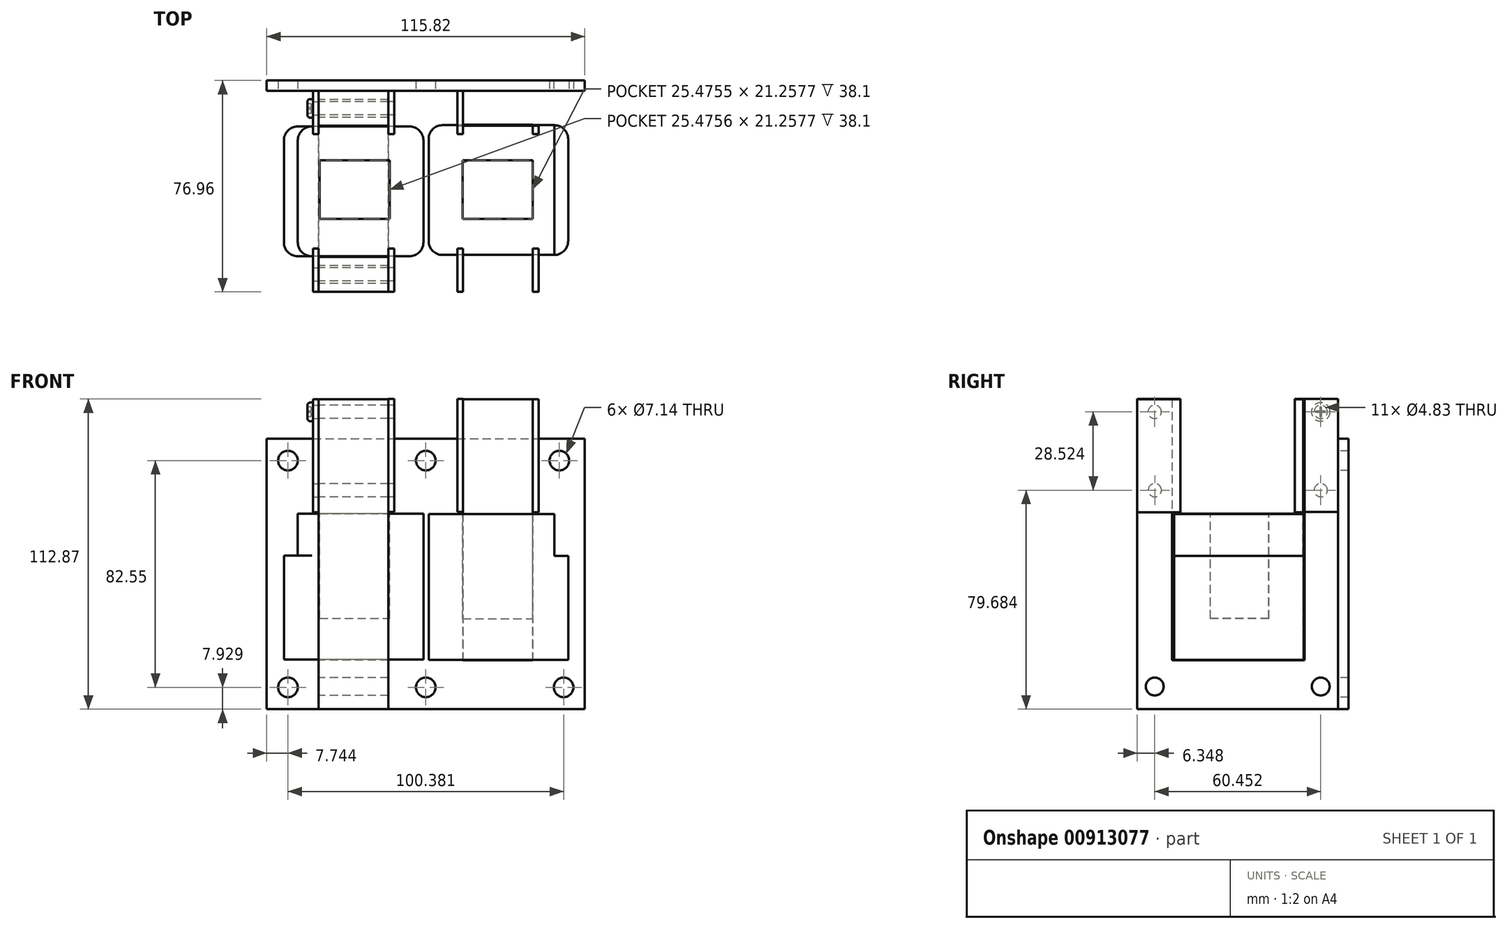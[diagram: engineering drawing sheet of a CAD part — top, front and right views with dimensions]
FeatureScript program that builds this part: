
annotation { "Feature Type Name" : "Feature", "Feature Type Description" : "" }
export const myFeature = defineFeature(function(context is Context, id is Id, definition is map)
    precondition{}
    {
        {
            var Q0;
            Q0=qCreatedBy(makeId("Front.planeOp"),FACE);
            var sketch = newSketch(context, id + "F0", { "sketchPlane" : qUnion([Q0])});
            skLineSegment(sketch, "E0", {"start": v(-55.41, 38.66) * mm, "end": v(60.41, 38.66) * mm});
            skLineSegment(sketch, "E1", {"start": v(60.41, 38.66) * mm, "end": v(60.41, -59.74) * mm});
            skLineSegment(sketch, "E2", {"start": v(60.41, -59.74) * mm, "end": v(-55.41, -59.74) * mm});
            skLineSegment(sketch, "E3", {"start": v(-55.41, 38.66) * mm, "end": v(-55.41, -59.74) * mm});
            skCircle(sketch, "E4", {"center": v(-47.67, -51.81) * mm, "radius": 3.57 * mm});
            skCircle(sketch, "E5", {"center": v(2.52, -51.81) * mm, "radius": 3.57 * mm});
            skCircle(sketch, "E6", {"center": v(52.71, -51.81) * mm, "radius": 3.57 * mm});
            skCircle(sketch, "E7", {"center": v(-47.67, 30.74) * mm, "radius": 3.57 * mm});
            skCircle(sketch, "E8", {"center": v(2.52, 30.74) * mm, "radius": 3.57 * mm});
            skCircle(sketch, "E9", {"center": v(51.17, 30.74) * mm, "radius": 3.57 * mm});
            skLineSegment(sketch, "E10.bottom", {"start": v(-36.46, -59.74) * mm, "end": v(-11.06, -59.74) * mm});
            skLineSegment(sketch, "E10.top", {"start": v(-36.46, 53.04) * mm, "end": v(-11.06, 53.04) * mm});
            skLineSegment(sketch, "E10.left", {"start": v(-36.46, -59.74) * mm, "end": v(-36.46, 53.04) * mm});
            skLineSegment(sketch, "E10.right", {"start": v(-11.06, -59.74) * mm, "end": v(-11.06, 53.04) * mm});
            skLineSegment(sketch, "E11.bottom", {"start": v(16.11, -59.74) * mm, "end": v(41.51, -59.74) * mm});
            skLineSegment(sketch, "E11.top", {"start": v(16.11, 53.04) * mm, "end": v(41.51, 53.04) * mm});
            skLineSegment(sketch, "E11.left", {"start": v(16.11, -59.74) * mm, "end": v(16.11, 53.04) * mm});
            skLineSegment(sketch, "E11.right", {"start": v(41.51, -59.74) * mm, "end": v(41.51, 53.04) * mm});
            skSolve(sketch);
        }
        {
            var Q0;
            {var subQ5=sQuery(id+"F0.wireOp",EDGE,"E10.top");Q0=makeQuery(id+"F0.imprint","IMPRINT",FACE,{"disambiguationData":[TD([[makeQuery(id+"F0.imprint","IMPRINT",EDGE,{"derivedFrom":subQ5}),-1.0]])]});}
            var Q1;
            {var subQ0=sQuery(id+"F0.wireOp",EDGE,"E10.right");var subQ1=sQuery(id+"F0.wireOp",EDGE,"E0");var subQ2=makeQuery(id+"F0.imprint","INTERSECT",VERTEX,{"derivedFrom":[subQ1,subQ0]});Q1=makeQuery(id+"F0.imprint","IMPRINT",FACE,{"disambiguationData":[TD([[makeQuery(id+"F0.imprint","IMPRINT",EDGE,{"disambiguationData":[TD([[subQ2,1.0]])],"derivedFrom":subQ1}),-1.0]])]});}
            var Q2;
            {var subQ0=sQuery(id+"F0.wireOp",EDGE,"E11.left");var subQ1=sQuery(id+"F0.wireOp",EDGE,"E0");var subQ2=makeQuery(id+"F0.imprint","INTERSECT",VERTEX,{"derivedFrom":[subQ1,subQ0]});Q2=makeQuery(id+"F0.imprint","IMPRINT",FACE,{"disambiguationData":[TD([[makeQuery(id+"F0.imprint","IMPRINT",EDGE,{"disambiguationData":[TD([[subQ2,-1.0]])],"derivedFrom":subQ1}),-1.0]])]});}
            var Q3;
            {var subQ5=sQuery(id+"F0.wireOp",EDGE,"E11.top");Q3=makeQuery(id+"F0.imprint","IMPRINT",FACE,{"disambiguationData":[TD([[makeQuery(id+"F0.imprint","IMPRINT",EDGE,{"derivedFrom":subQ5}),-1.0]])]});}
            extrude(context, id + "F1", {"entities" : qUnion([Q0, Q1, Q2, Q3]), "depth" : 73.15 * mm, "offsetDistance" : 25.4 * mm});
        }
        {
            var Q0;
            Q0=makeQuery(id+"F0.imprint","IMPRINT",FACE,{"disambiguationData":[TD([[makeQuery(id+"F0.imprint","IMPRINT",EDGE,{"derivedFrom":sQuery(id+"F0.wireOp",EDGE,"E5")}),-1.0]])]});
            var Q1;
            {var subQ1=sQuery(id+"F0.wireOp",EDGE,"E1");Q1=makeQuery(id+"F0.imprint","IMPRINT",FACE,{"disambiguationData":[TD([[makeQuery(id+"F0.imprint","IMPRINT",EDGE,{"derivedFrom":subQ1}),-1.0]])]});}
            var Q2;
            {var subQ0=sQuery(id+"F0.wireOp",EDGE,"E11.left");var subQ1=sQuery(id+"F0.wireOp",EDGE,"E0");var subQ2=makeQuery(id+"F0.imprint","INTERSECT",VERTEX,{"derivedFrom":[subQ1,subQ0]});Q2=makeQuery(id+"F0.imprint","IMPRINT",FACE,{"disambiguationData":[TD([[makeQuery(id+"F0.imprint","IMPRINT",EDGE,{"disambiguationData":[TD([[subQ2,-1.0]])],"derivedFrom":subQ1}),-1.0]])]});}
            var Q3;
            {var subQ0=sQuery(id+"F0.wireOp",EDGE,"E10.right");var subQ1=sQuery(id+"F0.wireOp",EDGE,"E0");var subQ2=makeQuery(id+"F0.imprint","INTERSECT",VERTEX,{"derivedFrom":[subQ1,subQ0]});Q3=makeQuery(id+"F0.imprint","IMPRINT",FACE,{"disambiguationData":[TD([[makeQuery(id+"F0.imprint","IMPRINT",EDGE,{"disambiguationData":[TD([[subQ2,1.0]])],"derivedFrom":subQ1}),-1.0]])]});}
            var Q4;
            {var subQ0=sQuery(id+"F0.wireOp",EDGE,"E3");Q4=makeQuery(id+"F0.imprint","IMPRINT",FACE,{"disambiguationData":[TD([[makeQuery(id+"F0.imprint","IMPRINT",EDGE,{"derivedFrom":subQ0}),1.0]])]});}
            extrude(context, id + "F2", {"entities" : qUnion([Q0, Q1, Q2, Q3, Q4]), "oppositeDirection" : true, "depth" : 3.8 * mm, "offsetDistance" : 25.4 * mm});
        }
        {
            var Q0;
            Q0=makeQuery(id+"F1.opExtrude","SWEPT_FACE",FACE,{"disambiguationData":[OSD([sQuery(id+"F0.wireOp",EDGE,"E10.left")])]});
            var sketch = newSketch(context, id + "F3", { "sketchPlane" : qUnion([Q0])});
            skLineSegment(sketch, "E12", {"start": v(12.7, 53.04) * mm, "end": v(12.7, -41.96) * mm});
            skLineSegment(sketch, "E13", {"start": v(12.7, -41.96) * mm, "end": v(60.45, -41.96) * mm});
            skLineSegment(sketch, "E14", {"start": v(60.45, 53.04) * mm, "end": v(60.45, -41.96) * mm});
            skLineSegment(sketch, "E15", {"start": v(60.45, 53.04) * mm, "end": v(12.7, 53.04) * mm});
            skLineSegment(sketch, "E16", {"start": v(12.7, 53.04) * mm, "end": v(60.45, 53.04) * mm});
            skCircle(sketch, "E17", {"center": v(6.35, 48.47) * mm, "radius": 2.41 * mm});
            skCircle(sketch, "E18", {"center": v(66.8, 48.47) * mm, "radius": 2.41 * mm});
            skCircle(sketch, "E19", {"center": v(6.35, 19.94) * mm, "radius": 2.41 * mm});
            skCircle(sketch, "E20", {"center": v(66.75, 19.94) * mm, "radius": 2.41 * mm});
            skCircle(sketch, "E21", {"center": v(6.35, -51.5) * mm, "radius": 3.25 * mm});
            skCircle(sketch, "E22", {"center": v(66.8, -51.5) * mm, "radius": 3.25 * mm});
            skSolve(sketch);
        }
        {
            var Q0;
            Q0=makeQuery(id+"F3.imprint","IMPRINT",FACE,{"disambiguationData":[TD([[makeQuery(id+"F3.imprint","IMPRINT",EDGE,{"derivedFrom":sQuery(id+"F3.wireOp",EDGE,"E12")}),1.0]])]});
            var Q1;
            Q1=makeQuery(id+"F3.imprint","IMPRINT",FACE,{"disambiguationData":[TD([[makeQuery(id+"F3.imprint","IMPRINT",EDGE,{"derivedFrom":sQuery(id+"F3.wireOp",EDGE,"E19")}),1.0]])]});
            var Q2;
            Q2=makeQuery(id+"F3.imprint","IMPRINT",FACE,{"disambiguationData":[TD([[makeQuery(id+"F3.imprint","IMPRINT",EDGE,{"derivedFrom":sQuery(id+"F3.wireOp",EDGE,"E20")}),1.0]])]});
            var Q3;
            Q3=makeQuery(id+"F3.imprint","IMPRINT",FACE,{"disambiguationData":[TD([[makeQuery(id+"F3.imprint","IMPRINT",EDGE,{"derivedFrom":sQuery(id+"F3.wireOp",EDGE,"E18")}),1.0]])]});
            var Q4;
            Q4=makeQuery(id+"F3.imprint","IMPRINT",FACE,{"disambiguationData":[TD([[makeQuery(id+"F3.imprint","IMPRINT",EDGE,{"derivedFrom":sQuery(id+"F3.wireOp",EDGE,"E17")}),1.0]])]});
            var Q5;
            Q5=makeQuery(id+"F3.imprint","IMPRINT",FACE,{"disambiguationData":[TD([[makeQuery(id+"F3.imprint","IMPRINT",EDGE,{"derivedFrom":sQuery(id+"F3.wireOp",EDGE,"E21")}),1.0]])]});
            var Q6;
            Q6=makeQuery(id+"F3.imprint","IMPRINT",FACE,{"disambiguationData":[TD([[makeQuery(id+"F3.imprint","IMPRINT",EDGE,{"derivedFrom":sQuery(id+"F3.wireOp",EDGE,"E22")}),1.0]])]});
            extrude(context, id + "F4", {"entities" : qUnion([Q0, Q1, Q2, Q3, Q4, Q5, Q6]), "operationType" : NewBodyOperationType.REMOVE, "endBound" : BoundingType.THROUGH_ALL, "oppositeDirection" : true, "depth" : 50.8 * mm, "offsetDistance" : 25.4 * mm});
        }
        {
            var Q0;
            Q0=makeQuery(id+"F1.opExtrude","SWEPT_FACE",FACE,{"disambiguationData":[OSD([sQuery(id+"F0.wireOp",EDGE,"E11.right")])]});
            var sketch = newSketch(context, id + "F5", { "sketchPlane" : qUnion([Q0])});
            skLineSegment(sketch, "E23", {"start": v(-60, 53.04) * mm, "end": v(-60, -41.96) * mm});
            skLineSegment(sketch, "E24", {"start": v(-60, -41.96) * mm, "end": v(-12.26, -41.96) * mm});
            skLineSegment(sketch, "E25", {"start": v(-12.26, -41.96) * mm, "end": v(-12.26, 53.04) * mm});
            skLineSegment(sketch, "E26", {"start": v(-12.26, 53.04) * mm, "end": v(-60, 53.04) * mm});
            skCircle(sketch, "E27", {"center": v(-66.8, 48.47) * mm, "radius": 2.41 * mm});
            skCircle(sketch, "E28", {"center": v(-6.35, 48.47) * mm, "radius": 2.41 * mm});
            skCircle(sketch, "E29", {"center": v(-66.8, 19.94) * mm, "radius": 2.41 * mm});
            skCircle(sketch, "E30", {"center": v(-6.35, 19.94) * mm, "radius": 2.41 * mm});
            skCircle(sketch, "E31", {"center": v(-66.8, -51.5) * mm, "radius": 3.25 * mm});
            skCircle(sketch, "E32", {"center": v(-6.35, -51.5) * mm, "radius": 3.25 * mm});
            skSolve(sketch);
        }
        {
            var Q0;
            Q0=makeQuery(id+"F5.imprint","IMPRINT",FACE,{"disambiguationData":[TD([[makeQuery(id+"F5.imprint","IMPRINT",EDGE,{"derivedFrom":sQuery(id+"F5.wireOp",EDGE,"E27")}),1.0]])]});
            var Q1;
            Q1=makeQuery(id+"F5.imprint","IMPRINT",FACE,{"disambiguationData":[TD([[makeQuery(id+"F5.imprint","IMPRINT",EDGE,{"derivedFrom":sQuery(id+"F5.wireOp",EDGE,"E29")}),1.0]])]});
            var Q2;
            Q2=makeQuery(id+"F5.imprint","IMPRINT",FACE,{"disambiguationData":[TD([[makeQuery(id+"F5.imprint","IMPRINT",EDGE,{"derivedFrom":sQuery(id+"F5.wireOp",EDGE,"E31")}),1.0]])]});
            var Q3;
            Q3=makeQuery(id+"F5.imprint","IMPRINT",FACE,{"disambiguationData":[TD([[makeQuery(id+"F5.imprint","IMPRINT",EDGE,{"derivedFrom":sQuery(id+"F5.wireOp",EDGE,"E32")}),1.0]])]});
            var Q4;
            Q4=makeQuery(id+"F5.imprint","IMPRINT",FACE,{"disambiguationData":[TD([[makeQuery(id+"F5.imprint","IMPRINT",EDGE,{"derivedFrom":sQuery(id+"F5.wireOp",EDGE,"E30")}),1.0]])]});
            var Q5;
            Q5=makeQuery(id+"F5.imprint","IMPRINT",FACE,{"disambiguationData":[TD([[makeQuery(id+"F5.imprint","IMPRINT",EDGE,{"derivedFrom":sQuery(id+"F5.wireOp",EDGE,"E28")}),1.0]])]});
            var Q6;
            Q6=makeQuery(id+"F5.imprint","IMPRINT",FACE,{"disambiguationData":[TD([[makeQuery(id+"F5.imprint","IMPRINT",EDGE,{"derivedFrom":sQuery(id+"F5.wireOp",EDGE,"E23")}),1.0]])]});
            extrude(context, id + "F6", {"entities" : qUnion([Q0, Q1, Q2, Q3, Q4, Q5, Q6]), "operationType" : NewBodyOperationType.REMOVE, "oppositeDirection" : true, "depth" : 25.4 * mm, "offsetDistance" : 25.4 * mm});
        }
        {
            var Q0;
            Q0=qCreatedBy(makeId("Right.planeOp"),FACE);
            cPlane(context, id + "F7", {"entities" : qUnion([Q0]), "cplaneType" : CPlaneType.OFFSET, "offset" : 23.75 * mm, "oppositeDirection" : true, "width" : 152.4 * mm, "height" : 152.4 * mm});
        }
        {
            var Q0;
            Q0=qCreatedBy(id+"F7.planeOp",FACE);
            var sketch = newSketch(context, id + "F8", { "sketchPlane" : qUnion([Q0])});
            skLineSegment(sketch, "E33.bottom", {"start": v(-12.93, 11.43) * mm, "end": v(-60.18, 11.43) * mm});
            skLineSegment(sketch, "E33.top", {"start": v(-12.93, -41.66) * mm, "end": v(-60.18, -41.66) * mm});
            skLineSegment(sketch, "E33.left", {"start": v(-12.93, 11.43) * mm, "end": v(-12.93, -41.66) * mm});
            skLineSegment(sketch, "E33.right", {"start": v(-60.18, 11.43) * mm, "end": v(-60.18, -41.66) * mm});
            skSolve(sketch);
        }
        {
            var Q0;
            Q0=makeQuery(id+"F8.imprint","IMPRINT",FACE,{"disambiguationData":[TD([[makeQuery(id+"F8.imprint","IMPRINT",EDGE,{"derivedFrom":sQuery(id+"F8.wireOp",EDGE,"E33.bottom")}),1.0]])]});
            extrude(context, id + "F9", {"entities" : qUnion([Q0]), "endBound" : BoundingType.SYMMETRIC, "depth" : 50.8 * mm, "offsetDistance" : 25.4 * mm});
        }
        {
            var Q0;
            Q0=makeQuery(id+"F9.opExtrude","CAP_FACE",FACE,{"disambiguationData":[OSD([sQuery(id+"F8.wireOp",EDGE,"E33.bottom"),sQuery(id+"F8.wireOp",EDGE,"E33.top"),sQuery(id+"F8.wireOp",EDGE,"E33.left"),sQuery(id+"F8.wireOp",EDGE,"E33.right")])],"isStart":true});
            var sketch = newSketch(context, id + "F10", { "sketchPlane" : qUnion([Q0])});
            skLineSegment(sketch, "E34.bottom", {"start": v(12.92, 11.43) * mm, "end": v(60.23, 11.43) * mm});
            skLineSegment(sketch, "E34.top", {"start": v(12.92, -3.8) * mm, "end": v(60.23, -3.8) * mm});
            skLineSegment(sketch, "E34.left", {"start": v(12.92, 11.43) * mm, "end": v(12.92, -3.8) * mm});
            skLineSegment(sketch, "E34.right", {"start": v(60.23, 11.43) * mm, "end": v(60.23, -3.8) * mm});
            skSolve(sketch);
        }
        {
            var Q0;
            Q0=makeQuery(id+"F10.imprint","IMPRINT",FACE,{"disambiguationData":[TD([[makeQuery(id+"F10.imprint","IMPRINT",EDGE,{"derivedFrom":sQuery(id+"F10.wireOp",EDGE,"E34.bottom")}),-1.0]])]});
            extrude(context, id + "F11", {"entities" : qUnion([Q0]), "operationType" : NewBodyOperationType.REMOVE, "oppositeDirection" : true, "depth" : 5.08 * mm, "offsetDistance" : 25.4 * mm});
        }
        {
            var Q0;
            Q0=makeQuery(id+"F9.opExtrude","CAP_EDGE",EDGE,{"disambiguationData":[OSD([sQuery(id+"F8.wireOp",EDGE,"E33.left")])],"isStart":true});
            var Q1;
            Q1=makeQuery(id+"F9.opExtrude","CAP_EDGE",EDGE,{"disambiguationData":[OSD([sQuery(id+"F8.wireOp",EDGE,"E33.right")])],"isStart":true});
            var Q2;
            Q2=makeQuery(id+"F9.opExtrude","CAP_EDGE",EDGE,{"disambiguationData":[OSD([sQuery(id+"F8.wireOp",EDGE,"E33.right")])],"isStart":false});
            var Q3;
            Q3=makeQuery(id+"F9.opExtrude","CAP_EDGE",EDGE,{"disambiguationData":[OSD([sQuery(id+"F8.wireOp",EDGE,"E33.left")])],"isStart":false});
            var Q4;
            Q4=makeQuery(id+"F11.boolean.opBoolean","INTERSECT",EDGE,{"derivedFrom":[makeQuery(id+"F9.opExtrude","SWEPT_FACE",FACE,{"disambiguationData":[OSD([sQuery(id+"F8.wireOp",EDGE,"E33.left")])]}),makeQuery(id+"F11.opExtrude","CAP_FACE",FACE,{"disambiguationData":[OSD([sQuery(id+"F10.wireOp",EDGE,"E34.bottom"),sQuery(id+"F10.wireOp",EDGE,"E34.top"),sQuery(id+"F10.wireOp",EDGE,"E34.left"),sQuery(id+"F10.wireOp",EDGE,"E34.right")])],"isStart":false})]});
            var Q5;
            Q5=makeQuery(id+"F11.boolean.opBoolean","INTERSECT",EDGE,{"derivedFrom":[makeQuery(id+"F9.opExtrude","SWEPT_FACE",FACE,{"disambiguationData":[OSD([sQuery(id+"F8.wireOp",EDGE,"E33.right")])]}),makeQuery(id+"F11.opExtrude","CAP_FACE",FACE,{"disambiguationData":[OSD([sQuery(id+"F10.wireOp",EDGE,"E34.bottom"),sQuery(id+"F10.wireOp",EDGE,"E34.top"),sQuery(id+"F10.wireOp",EDGE,"E34.left"),sQuery(id+"F10.wireOp",EDGE,"E34.right")])],"isStart":false})]});
            fillet(context, id + "F12", {"entities" : qUnion([Q0, Q1, Q2, Q3, Q4, Q5]), "radius" : 5.08 * mm, "tangentPropagation" : true, "allowEdgeOverflow" : false});
        }
        {
            var Q0;
            Q0=makeQuery(id+"F9.opExtrude","SWEPT_FACE",FACE,{"disambiguationData":[OSD([sQuery(id+"F8.wireOp",EDGE,"E33.bottom")])]});
            var sketch = newSketch(context, id + "F13", { "sketchPlane" : qUnion([Q0])});
            skLineSegment(sketch, "E35.bottom", {"start": v(-36.13, -25.29) * mm, "end": v(-10.65, -25.29) * mm});
            skLineSegment(sketch, "E35.top", {"start": v(-36.13, -46.55) * mm, "end": v(-10.65, -46.55) * mm});
            skLineSegment(sketch, "E35.left", {"start": v(-36.13, -25.29) * mm, "end": v(-36.13, -46.55) * mm});
            skLineSegment(sketch, "E35.right", {"start": v(-10.65, -25.29) * mm, "end": v(-10.65, -46.55) * mm});
            skSolve(sketch);
        }
        {
            var Q0;
            Q0=makeQuery(id+"F13.imprint","IMPRINT",FACE,{"disambiguationData":[TD([[makeQuery(id+"F13.imprint","IMPRINT",EDGE,{"derivedFrom":sQuery(id+"F13.wireOp",EDGE,"E35.bottom")}),-1.0]])]});
            extrude(context, id + "F14", {"entities" : qUnion([Q0]), "operationType" : NewBodyOperationType.REMOVE, "oppositeDirection" : true, "depth" : 38.1 * mm, "offsetDistance" : 25.4 * mm});
        }
        {
            var Q0;
            Q0=qCreatedBy(makeId("Right.planeOp"),FACE);
            cPlane(context, id + "F15", {"entities" : qUnion([Q0]), "cplaneType" : CPlaneType.OFFSET, "offset" : 28.96 * mm, "width" : 152.4 * mm, "height" : 152.4 * mm});
        }
        {
            var Q0;
            Q0=qCreatedBy(id+"F15.planeOp",FACE);
            var sketch = newSketch(context, id + "F16", { "sketchPlane" : qUnion([Q0])});
            skLineSegment(sketch, "E36.bottom", {"start": v(-12.45, 11.3) * mm, "end": v(-59.7, 11.3) * mm});
            skLineSegment(sketch, "E36.top", {"start": v(-12.45, -41.78) * mm, "end": v(-59.7, -41.78) * mm});
            skLineSegment(sketch, "E36.left", {"start": v(-12.45, 11.3) * mm, "end": v(-12.45, -41.78) * mm});
            skLineSegment(sketch, "E36.right", {"start": v(-59.7, 11.3) * mm, "end": v(-59.7, -41.78) * mm});
            skSolve(sketch);
        }
        {
            var Q0;
            Q0=makeQuery(id+"F16.imprint","IMPRINT",FACE,{"disambiguationData":[TD([[makeQuery(id+"F16.imprint","IMPRINT",EDGE,{"derivedFrom":sQuery(id+"F16.wireOp",EDGE,"E36.bottom")}),1.0]])]});
            extrude(context, id + "F17", {"entities" : qUnion([Q0]), "endBound" : BoundingType.SYMMETRIC, "depth" : 50.8 * mm, "offsetDistance" : 25.4 * mm});
        }
        {
            var Q0;
            Q0=makeQuery(id+"F17.opExtrude","CAP_FACE",FACE,{"disambiguationData":[OSD([sQuery(id+"F16.wireOp",EDGE,"E36.bottom"),sQuery(id+"F16.wireOp",EDGE,"E36.top"),sQuery(id+"F16.wireOp",EDGE,"E36.left"),sQuery(id+"F16.wireOp",EDGE,"E36.right")])],"isStart":false});
            var sketch = newSketch(context, id + "F18", { "sketchPlane" : qUnion([Q0])});
            skLineSegment(sketch, "E37.bottom", {"start": v(-59.7, 11.3) * mm, "end": v(-12.45, 11.3) * mm});
            skLineSegment(sketch, "E37.top", {"start": v(-59.7, -3.94) * mm, "end": v(-12.45, -3.94) * mm});
            skLineSegment(sketch, "E37.left", {"start": v(-59.7, 11.3) * mm, "end": v(-59.7, -3.94) * mm});
            skLineSegment(sketch, "E37.right", {"start": v(-12.45, 11.3) * mm, "end": v(-12.45, -3.94) * mm});
            skSolve(sketch);
        }
        {
            var Q0;
            Q0=makeQuery(id+"F18.imprint","IMPRINT",FACE,{"disambiguationData":[TD([[makeQuery(id+"F18.imprint","IMPRINT",EDGE,{"derivedFrom":sQuery(id+"F18.wireOp",EDGE,"E37.bottom")}),1.0]])]});
            extrude(context, id + "F19", {"entities" : qUnion([Q0]), "operationType" : NewBodyOperationType.REMOVE, "oppositeDirection" : true, "depth" : 5.08 * mm, "offsetDistance" : 25.4 * mm});
        }
        {
            var Q0;
            Q0=makeQuery(id+"F17.opExtrude","CAP_EDGE",EDGE,{"disambiguationData":[OSD([sQuery(id+"F16.wireOp",EDGE,"E36.right")])],"isStart":false});
            var Q1;
            Q1=makeQuery(id+"F17.opExtrude","CAP_EDGE",EDGE,{"disambiguationData":[OSD([sQuery(id+"F16.wireOp",EDGE,"E36.left")])],"isStart":false});
            var Q2;
            Q2=makeQuery(id+"F19.boolean.opBoolean","COPY",EDGE,{"derivedFrom":makeQuery(id+"F19.opExtrude","CAP_EDGE",EDGE,{"disambiguationData":[OSD([sQuery(id+"F18.wireOp",EDGE,"E37.right")])],"isStart":false})});
            var Q3;
            Q3=makeQuery(id+"F19.boolean.opBoolean","COPY",EDGE,{"derivedFrom":makeQuery(id+"F19.opExtrude","CAP_EDGE",EDGE,{"disambiguationData":[OSD([sQuery(id+"F18.wireOp",EDGE,"E37.left")])],"isStart":false})});
            var Q4;
            Q4=makeQuery(id+"F17.opExtrude","CAP_EDGE",EDGE,{"disambiguationData":[OSD([sQuery(id+"F16.wireOp",EDGE,"E36.right")])],"isStart":true});
            var Q5;
            Q5=makeQuery(id+"F17.opExtrude","CAP_EDGE",EDGE,{"disambiguationData":[OSD([sQuery(id+"F16.wireOp",EDGE,"E36.left")])],"isStart":true});
            fillet(context, id + "F20", {"entities" : qUnion([Q0, Q1, Q2, Q3, Q4, Q5]), "radius" : 5.08 * mm, "tangentPropagation" : true, "allowEdgeOverflow" : false});
        }
        {
            var Q0;
            Q0=makeQuery(id+"F17.opExtrude","SWEPT_FACE",FACE,{"disambiguationData":[OSD([sQuery(id+"F16.wireOp",EDGE,"E36.bottom")])]});
            var sketch = newSketch(context, id + "F21", { "sketchPlane" : qUnion([Q0])});
            skLineSegment(sketch, "E38.bottom", {"start": v(16, -25.26) * mm, "end": v(41.48, -25.26) * mm});
            skLineSegment(sketch, "E38.top", {"start": v(16, -46.52) * mm, "end": v(41.48, -46.52) * mm});
            skLineSegment(sketch, "E38.left", {"start": v(16, -25.26) * mm, "end": v(16, -46.52) * mm});
            skLineSegment(sketch, "E38.right", {"start": v(41.48, -25.26) * mm, "end": v(41.48, -46.52) * mm});
            skSolve(sketch);
        }
        {
            var Q0;
            Q0=makeQuery(id+"F21.imprint","IMPRINT",FACE,{"disambiguationData":[TD([[makeQuery(id+"F21.imprint","IMPRINT",EDGE,{"derivedFrom":sQuery(id+"F21.wireOp",EDGE,"E38.bottom")}),-1.0]])]});
            extrude(context, id + "F22", {"entities" : qUnion([Q0]), "operationType" : NewBodyOperationType.REMOVE, "oppositeDirection" : true, "depth" : 38.1 * mm, "offsetDistance" : 25.4 * mm});
        }
        {
            var Q0;
            Q0=makeQuery(id+"F1.opExtrude","SWEPT_FACE",FACE,{"disambiguationData":[OSD([sQuery(id+"F0.wireOp",EDGE,"E10.left")])]});
            var sketch = newSketch(context, id + "F23", { "sketchPlane" : qUnion([Q0])});
            skLineSegment(sketch, "E39.bottom", {"start": v(57.4, 53.04) * mm, "end": v(73.15, 53.04) * mm});
            skLineSegment(sketch, "E39.top", {"start": v(57.4, 11.93) * mm, "end": v(73.15, 11.93) * mm});
            skLineSegment(sketch, "E39.left", {"start": v(57.4, 53.04) * mm, "end": v(57.4, 11.93) * mm});
            skLineSegment(sketch, "E39.right", {"start": v(73.15, 53.04) * mm, "end": v(73.15, 11.93) * mm});
            skLineSegment(sketch, "E40.bottom", {"start": v(0, 53.04) * mm, "end": v(15.75, 53.04) * mm});
            skLineSegment(sketch, "E40.top", {"start": v(0, 12) * mm, "end": v(15.75, 12) * mm});
            skLineSegment(sketch, "E40.left", {"start": v(0, 53.04) * mm, "end": v(0, 12) * mm});
            skLineSegment(sketch, "E40.right", {"start": v(15.75, 53.04) * mm, "end": v(15.75, 12) * mm});
            skSolve(sketch);
        }
        {
            var Q0;
            {var subQ0=sQuery(id+"F23.wireOp",EDGE,"E40.left");Q0=makeQuery(id+"F23.imprint","IMPRINT",FACE,{"disambiguationData":[TD([[makeQuery(id+"F23.imprint","IMPRINT",EDGE,{"derivedFrom":subQ0}),-1.0]])]});}
            var Q1;
            {var subQ3=sQuery(id+"F23.wireOp",EDGE,"E40.right");Q1=makeQuery(id+"F23.imprint","IMPRINT",FACE,{"disambiguationData":[TD([[makeQuery(id+"F23.imprint","IMPRINT",EDGE,{"derivedFrom":subQ3}),-1.0]])]});}
            var Q2;
            {var subQ0=sQuery(id+"F23.wireOp",EDGE,"E39.right");Q2=makeQuery(id+"F23.imprint","IMPRINT",FACE,{"disambiguationData":[TD([[makeQuery(id+"F23.imprint","IMPRINT",EDGE,{"derivedFrom":subQ0}),1.0]])]});}
            var Q3;
            {var subQ3=sQuery(id+"F23.wireOp",EDGE,"E39.left");Q3=makeQuery(id+"F23.imprint","IMPRINT",FACE,{"disambiguationData":[TD([[makeQuery(id+"F23.imprint","IMPRINT",EDGE,{"derivedFrom":subQ3}),1.0]])]});}
            extrude(context, id + "F24", {"entities" : qUnion([Q0, Q1, Q2, Q3]), "depth" : 2.1 * mm, "offsetDistance" : 25.4 * mm});
        }
        {
            var Q0;
            Q0=makeQuery(id+"F1.opExtrude","SWEPT_FACE",FACE,{"disambiguationData":[OSD([sQuery(id+"F0.wireOp",EDGE,"E10.right")])]});
            var sketch = newSketch(context, id + "F25", { "sketchPlane" : qUnion([Q0])});
            skLineSegment(sketch, "E41.bottom", {"start": v(-15.75, 53.13) * mm, "end": v(0, 53.13) * mm});
            skLineSegment(sketch, "E41.top", {"start": v(-15.75, 12.02) * mm, "end": v(0, 12.02) * mm});
            skLineSegment(sketch, "E41.left", {"start": v(-15.75, 53.13) * mm, "end": v(-15.75, 12.02) * mm});
            skLineSegment(sketch, "E41.right", {"start": v(0, 53.13) * mm, "end": v(0, 12.02) * mm});
            skLineSegment(sketch, "E42.bottom", {"start": v(-73.15, 53.13) * mm, "end": v(-57.4, 53.13) * mm});
            skLineSegment(sketch, "E42.top", {"start": v(-73.15, 12.1) * mm, "end": v(-57.4, 12.1) * mm});
            skLineSegment(sketch, "E42.left", {"start": v(-73.15, 53.13) * mm, "end": v(-73.15, 12.1) * mm});
            skLineSegment(sketch, "E42.right", {"start": v(-57.4, 53.13) * mm, "end": v(-57.4, 12.1) * mm});
            skSolve(sketch);
        }
        {
            var Q0;
            {var subQ0=sQuery(id+"F0.wireOp",EDGE,"E10.right");var subQ1=makeQuery(id+"F1.opExtrude","SWEPT_FACE",FACE,{"disambiguationData":[OSD([subQ0])]});Q0=makeQuery(id+"F25.imprint","IMPRINT",FACE,{"disambiguationData":[TD([[makeQuery(id+"F25.imprint","IMPRINT",EDGE,{"derivedFrom":makeQuery(id+"F4.boolean.opBoolean","INTERSECT",EDGE,{"derivedFrom":[subQ1,makeQuery(id+"F4.opExtrude","SWEPT_FACE",FACE,{"disambiguationData":[OSD([sQuery(id+"F3.wireOp",EDGE,"E18")])]})]})}),1.0]])]});}
            var Q1;
            {var subQ6=sQuery(id+"F25.wireOp",EDGE,"E42.bottom");Q1=makeQuery(id+"F25.imprint","IMPRINT",FACE,{"disambiguationData":[TD([[makeQuery(id+"F25.imprint","IMPRINT",EDGE,{"derivedFrom":subQ6}),-1.0]])]});}
            var Q2;
            {var subQ6=sQuery(id+"F25.wireOp",EDGE,"E41.bottom");Q2=makeQuery(id+"F25.imprint","IMPRINT",FACE,{"disambiguationData":[TD([[makeQuery(id+"F25.imprint","IMPRINT",EDGE,{"derivedFrom":subQ6}),-1.0]])]});}
            var Q3;
            {var subQ0=sQuery(id+"F0.wireOp",EDGE,"E10.right");var subQ1=makeQuery(id+"F1.opExtrude","SWEPT_FACE",FACE,{"disambiguationData":[OSD([subQ0])]});Q3=makeQuery(id+"F25.imprint","IMPRINT",FACE,{"disambiguationData":[TD([[makeQuery(id+"F25.imprint","IMPRINT",EDGE,{"derivedFrom":makeQuery(id+"F4.boolean.opBoolean","INTERSECT",EDGE,{"derivedFrom":[subQ1,makeQuery(id+"F4.opExtrude","SWEPT_FACE",FACE,{"disambiguationData":[OSD([sQuery(id+"F3.wireOp",EDGE,"E17")])]})]})}),1.0]])]});}
            extrude(context, id + "F26", {"entities" : qUnion([Q0, Q1, Q2, Q3]), "depth" : 2.1 * mm, "offsetDistance" : 25.4 * mm});
        }
        {
            var Q0;
            Q0=makeQuery(id+"F1.opExtrude","SWEPT_FACE",FACE,{"disambiguationData":[OSD([sQuery(id+"F0.wireOp",EDGE,"E11.left")])]});
            var sketch = newSketch(context, id + "F27", { "sketchPlane" : qUnion([Q0])});
            skLineSegment(sketch, "E43.bottom", {"start": v(57.4, 53.13) * mm, "end": v(73.15, 53.13) * mm});
            skLineSegment(sketch, "E43.top", {"start": v(57.4, 12.02) * mm, "end": v(73.15, 12.02) * mm});
            skLineSegment(sketch, "E43.left", {"start": v(57.4, 53.13) * mm, "end": v(57.4, 12.02) * mm});
            skLineSegment(sketch, "E43.right", {"start": v(73.15, 53.13) * mm, "end": v(73.15, 12.02) * mm});
            skLineSegment(sketch, "E44.bottom", {"start": v(0, 53.13) * mm, "end": v(15.75, 53.13) * mm});
            skLineSegment(sketch, "E44.top", {"start": v(0, 12.1) * mm, "end": v(15.75, 12.1) * mm});
            skLineSegment(sketch, "E44.left", {"start": v(0, 53.13) * mm, "end": v(0, 12.1) * mm});
            skLineSegment(sketch, "E44.right", {"start": v(15.75, 53.13) * mm, "end": v(15.75, 12.1) * mm});
            skSolve(sketch);
        }
        {
            var Q0;
            Q0=makeQuery(id+"F27.imprint","IMPRINT",FACE,{"disambiguationData":[TD([[makeQuery(id+"F27.imprint","IMPRINT",EDGE,{"derivedFrom":makeQuery(id+"F6.boolean.opBoolean","COPY",EDGE,{"derivedFrom":makeQuery(id+"F6.opExtrude","CAP_EDGE",EDGE,{"disambiguationData":[OSD([sQuery(id+"F5.wireOp",EDGE,"E28")])],"isStart":false})})}),1.0]])]});
            var Q1;
            {var subQ5=sQuery(id+"F27.wireOp",EDGE,"E44.bottom");Q1=makeQuery(id+"F27.imprint","IMPRINT",FACE,{"disambiguationData":[TD([[makeQuery(id+"F27.imprint","IMPRINT",EDGE,{"derivedFrom":subQ5}),-1.0]])]});}
            var Q2;
            {var subQ5=sQuery(id+"F27.wireOp",EDGE,"E43.bottom");Q2=makeQuery(id+"F27.imprint","IMPRINT",FACE,{"disambiguationData":[TD([[makeQuery(id+"F27.imprint","IMPRINT",EDGE,{"derivedFrom":subQ5}),-1.0]])]});}
            var Q3;
            Q3=makeQuery(id+"F27.imprint","IMPRINT",FACE,{"disambiguationData":[TD([[makeQuery(id+"F27.imprint","IMPRINT",EDGE,{"derivedFrom":makeQuery(id+"F6.boolean.opBoolean","COPY",EDGE,{"derivedFrom":makeQuery(id+"F6.opExtrude","CAP_EDGE",EDGE,{"disambiguationData":[OSD([sQuery(id+"F5.wireOp",EDGE,"E27")])],"isStart":false})})}),1.0]])]});
            extrude(context, id + "F28", {"entities" : qUnion([Q0, Q1, Q2, Q3]), "depth" : 2.1 * mm, "offsetDistance" : 25.4 * mm});
        }
        {
            var Q0;
            Q0=makeQuery(id+"F1.opExtrude","SWEPT_FACE",FACE,{"disambiguationData":[OSD([sQuery(id+"F0.wireOp",EDGE,"E11.right")])]});
            var sketch = newSketch(context, id + "F29", { "sketchPlane" : qUnion([Q0])});
            skLineSegment(sketch, "E45.bottom", {"start": v(-15.75, 53) * mm, "end": v(0, 53) * mm});
            skLineSegment(sketch, "E45.top", {"start": v(-15.75, 11.9) * mm, "end": v(0, 11.9) * mm});
            skLineSegment(sketch, "E45.left", {"start": v(-15.75, 53) * mm, "end": v(-15.75, 11.9) * mm});
            skLineSegment(sketch, "E45.right", {"start": v(0, 53) * mm, "end": v(0, 11.9) * mm});
            skLineSegment(sketch, "E46.bottom", {"start": v(-73.15, 53) * mm, "end": v(-57.4, 53) * mm});
            skLineSegment(sketch, "E46.top", {"start": v(-73.15, 11.97) * mm, "end": v(-57.4, 11.97) * mm});
            skLineSegment(sketch, "E46.left", {"start": v(-73.15, 53) * mm, "end": v(-73.15, 11.97) * mm});
            skLineSegment(sketch, "E46.right", {"start": v(-57.4, 53) * mm, "end": v(-57.4, 11.97) * mm});
            skSolve(sketch);
        }
        {
            var Q0;
            {var subQ0=sQuery(id+"F29.wireOp",EDGE,"E46.left");Q0=makeQuery(id+"F29.imprint","IMPRINT",FACE,{"disambiguationData":[TD([[makeQuery(id+"F29.imprint","IMPRINT",EDGE,{"derivedFrom":subQ0}),-1.0]])]});}
            var Q1;
            {var subQ0=sQuery(id+"F29.wireOp",EDGE,"E46.right");Q1=makeQuery(id+"F29.imprint","IMPRINT",FACE,{"disambiguationData":[TD([[makeQuery(id+"F29.imprint","IMPRINT",EDGE,{"derivedFrom":subQ0}),-1.0]])]});}
            var Q2;
            {var subQ0=sQuery(id+"F29.wireOp",EDGE,"E45.left");Q2=makeQuery(id+"F29.imprint","IMPRINT",FACE,{"disambiguationData":[TD([[makeQuery(id+"F29.imprint","IMPRINT",EDGE,{"derivedFrom":subQ0}),1.0]])]});}
            var Q3;
            {var subQ0=sQuery(id+"F29.wireOp",EDGE,"E45.right");Q3=makeQuery(id+"F29.imprint","IMPRINT",FACE,{"disambiguationData":[TD([[makeQuery(id+"F29.imprint","IMPRINT",EDGE,{"derivedFrom":subQ0}),1.0]])]});}
            extrude(context, id + "F30", {"entities" : qUnion([Q0, Q1, Q2, Q3]), "depth" : 2.1 * mm, "offsetDistance" : 25.4 * mm});
        }
        {
            var Q0;
            Q0=makeQuery(id+"F24.opExtrude","CAP_FACE",FACE,{"disambiguationData":[OSD([sQuery(id+"F3.wireOp",EDGE,"E17"),sQuery(id+"F3.wireOp",EDGE,"E19"),sQuery(id+"F23.wireOp",EDGE,"E40.bottom"),sQuery(id+"F23.wireOp",EDGE,"E40.top"),sQuery(id+"F23.wireOp",EDGE,"E40.left"),sQuery(id+"F23.wireOp",EDGE,"E40.right")])],"isStart":false});
            var sketch = newSketch(context, id + "F31", { "sketchPlane" : qUnion([Q0])});
            skCircle(sketch, "E47", {"center": v(6.35, 48.47) * mm, "radius": 3.39 * mm});
            skSolve(sketch);
        }
        {
            var Q0;
            Q0=makeQuery(id+"F31.imprint","IMPRINT",FACE,{"disambiguationData":[TD([[makeQuery(id+"F31.imprint","IMPRINT",EDGE,{"derivedFrom":sQuery(id+"F31.wireOp",EDGE,"E47")}),1.0]])]});
            var Q1;
            Q1=makeQuery(id+"F31.imprint","IMPRINT",FACE,{"disambiguationData":[TD([[makeQuery(id+"F31.imprint","IMPRINT",EDGE,{"derivedFrom":makeQuery(id+"F24.opExtrude","CAP_EDGE",EDGE,{"disambiguationData":[OSD([sQuery(id+"F3.wireOp",EDGE,"E17")])],"isStart":false})}),1.0]])]});
            extrude(context, id + "F32", {"entities" : qUnion([Q0, Q1]), "operationType" : NewBodyOperationType.ADD, "depth" : 2.03 * mm, "offsetDistance" : 25.4 * mm});
        }
        {
            var Q0;
            Q0=makeQuery(id+"F32.opExtrude","CAP_EDGE",EDGE,{"disambiguationData":[OSD([sQuery(id+"F31.wireOp",EDGE,"E47")])],"isStart":false});
            fillet(context, id + "F33", {"entities" : qUnion([Q0]), "radius" : 1.02 * mm, "tangentPropagation" : true, "allowEdgeOverflow" : false});
        }
        {
            var Q0;
            Q0=makeQuery(id+"F32.opExtrude","CAP_FACE",FACE,{"disambiguationData":[OSD([sQuery(id+"F31.wireOp",EDGE,"E47")])],"isStart":false});
            var sketch = newSketch(context, id + "F34", { "sketchPlane" : qUnion([Q0])});
            skLineSegment(sketch, "E48.bottom", {"start": v(6.1, 50.22) * mm, "end": v(6.64, 50.22) * mm});
            skLineSegment(sketch, "E48.top", {"start": v(6.1, 46.67) * mm, "end": v(6.64, 46.67) * mm});
            skLineSegment(sketch, "E48.left", {"start": v(6.1, 50.22) * mm, "end": v(6.1, 46.67) * mm});
            skLineSegment(sketch, "E48.right", {"start": v(6.64, 50.22) * mm, "end": v(6.64, 46.67) * mm});
            skLineSegment(sketch, "E49.bottom", {"start": v(4.64, 48.2) * mm, "end": v(4.64, 48.75) * mm});
            skLineSegment(sketch, "E49.top", {"start": v(8.2, 48.2) * mm, "end": v(8.2, 48.75) * mm});
            skLineSegment(sketch, "E49.left", {"start": v(4.64, 48.2) * mm, "end": v(8.2, 48.2) * mm});
            skLineSegment(sketch, "E49.right", {"start": v(4.64, 48.75) * mm, "end": v(8.2, 48.75) * mm});
            skSolve(sketch);
        }
        {
            var Q0;
            {var subQ5=sQuery(id+"F34.wireOp",EDGE,"E49.top");Q0=makeQuery(id+"F34.imprint","IMPRINT",FACE,{"disambiguationData":[TD([[makeQuery(id+"F34.imprint","IMPRINT",EDGE,{"derivedFrom":subQ5}),1.0]])]});}
            var Q1;
            {var subQ0=sQuery(id+"F34.wireOp",EDGE,"E49.right");var subQ1=sQuery(id+"F34.wireOp",EDGE,"E48.left");var subQ2=makeQuery(id+"F34.imprint","INTERSECT",VERTEX,{"derivedFrom":[subQ1,subQ0]});Q1=makeQuery(id+"F34.imprint","IMPRINT",FACE,{"disambiguationData":[TD([[makeQuery(id+"F34.imprint","IMPRINT",EDGE,{"disambiguationData":[TD([[subQ2,-1.0]])],"derivedFrom":subQ1}),1.0]])]});}
            var Q2;
            {var subQ0=sQuery(id+"F34.wireOp",EDGE,"E48.bottom");Q2=makeQuery(id+"F34.imprint","IMPRINT",FACE,{"disambiguationData":[TD([[makeQuery(id+"F34.imprint","IMPRINT",EDGE,{"derivedFrom":subQ0}),-1.0]])]});}
            var Q3;
            {var subQ5=sQuery(id+"F34.wireOp",EDGE,"E49.bottom");Q3=makeQuery(id+"F34.imprint","IMPRINT",FACE,{"disambiguationData":[TD([[makeQuery(id+"F34.imprint","IMPRINT",EDGE,{"derivedFrom":subQ5}),-1.0]])]});}
            var Q4;
            {var subQ0=sQuery(id+"F34.wireOp",EDGE,"E48.top");Q4=makeQuery(id+"F34.imprint","IMPRINT",FACE,{"disambiguationData":[TD([[makeQuery(id+"F34.imprint","IMPRINT",EDGE,{"derivedFrom":subQ0}),1.0]])]});}
            extrude(context, id + "F35", {"entities" : qUnion([Q0, Q1, Q2, Q3, Q4]), "operationType" : NewBodyOperationType.REMOVE, "oppositeDirection" : true, "depth" : 1.27 * mm, "offsetDistance" : 25.4 * mm});
        }
    });
